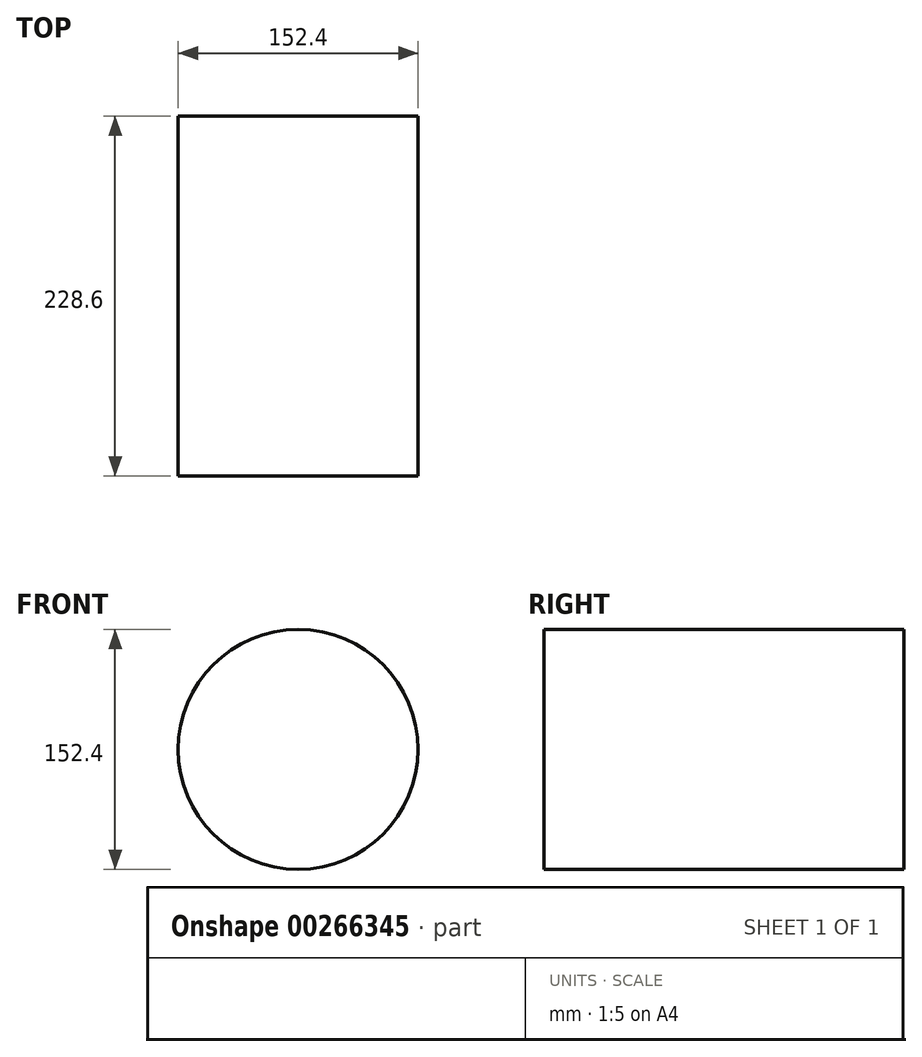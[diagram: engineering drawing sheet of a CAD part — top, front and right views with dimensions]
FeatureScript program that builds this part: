
annotation { "Feature Type Name" : "Feature", "Feature Type Description" : "" }
export const myFeature = defineFeature(function(context is Context, id is Id, definition is map)
    precondition{}
    {
        {
            var Q0;
            Q0=qCreatedBy(makeId("Front.planeOp"),FACE);
            var sketch = newSketch(context, id + "F0", { "sketchPlane" : qUnion([Q0])});
            skCircle(sketch, "E0", {"center": v(0, 0) * mm, "radius": 76.2 * mm});
            skSolve(sketch);
        }
        {
            var Q0;
            Q0=makeQuery(id+"F0.imprint","IMPRINT",FACE,{"disambiguationData":[TD([[makeQuery(id+"F0.imprint","IMPRINT",EDGE,{"derivedFrom":sQuery(id+"F0.wireOp",EDGE,"E0")}),1.0]])]});
            extrude(context, id + "F1", {"entities" : qUnion([Q0]), "depth" : 228.6 * mm});
        }
    });
